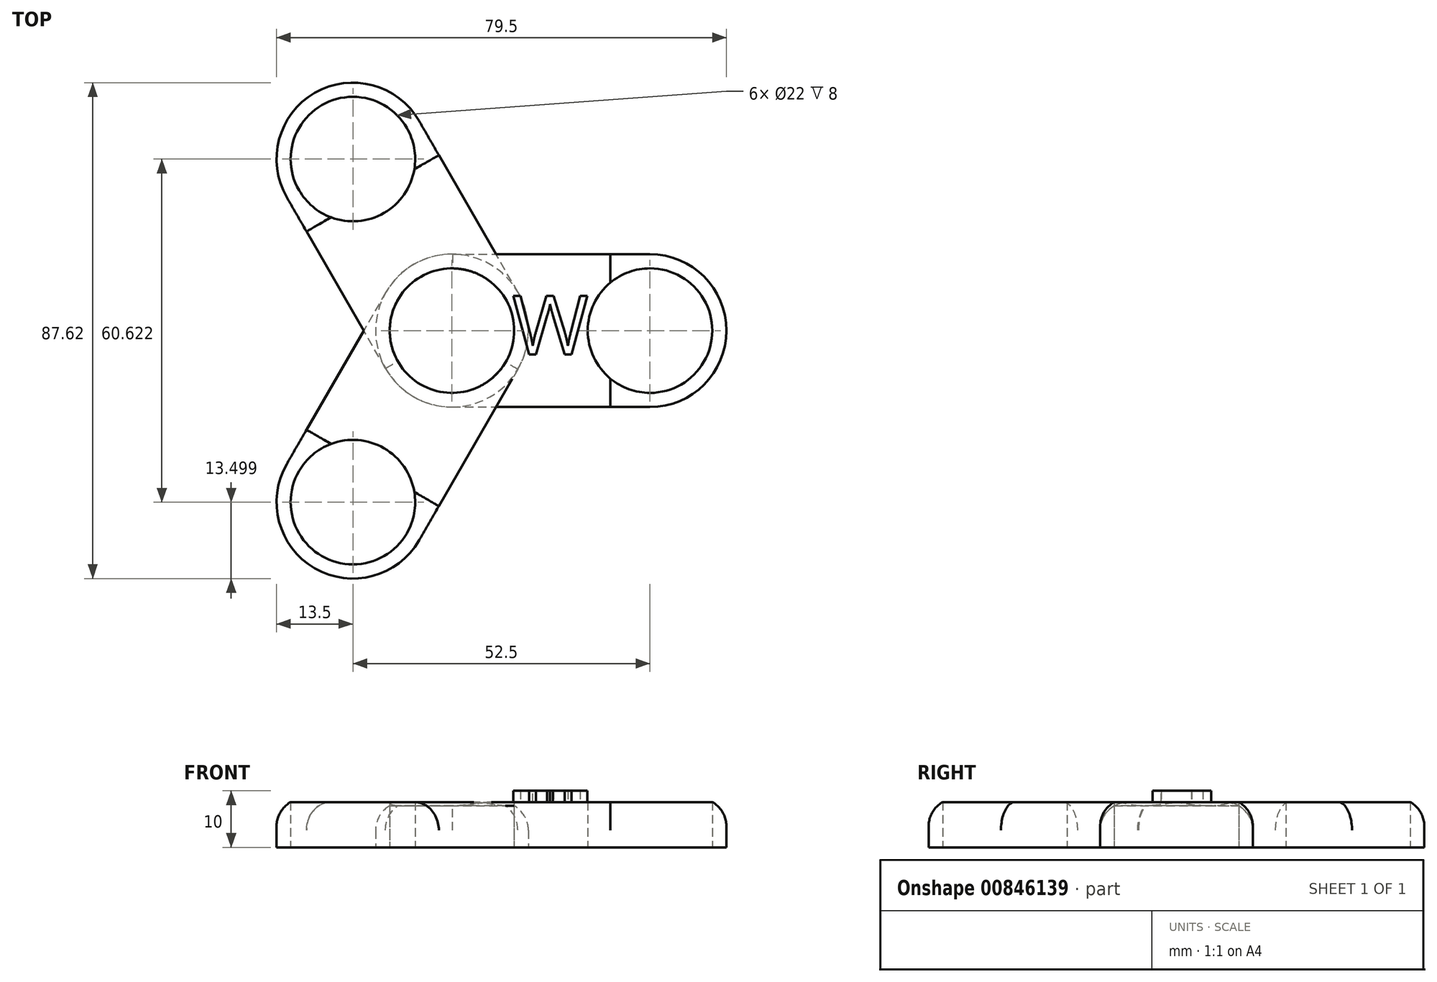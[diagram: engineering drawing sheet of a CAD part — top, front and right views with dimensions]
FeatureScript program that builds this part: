
annotation { "Feature Type Name" : "Feature", "Feature Type Description" : "" }
export const myFeature = defineFeature(function(context is Context, id is Id, definition is map)
    precondition{}
    {
        {
            var Q0;
            Q0=qCreatedBy(makeId("Top.planeOp"),FACE);
            var sketch = newSketch(context, id + "F0", { "sketchPlane" : qUnion([Q0])});
            skCircle(sketch, "E0", {"center": v(0, 0) * mm, "radius": 11 * mm});
            skCircle(sketch, "E1", {"center": v(0, 0) * mm, "radius": 13.5 * mm});
            skLineSegment(sketch, "E2", {"start": v(0, 0) * mm, "end": v(35, 0) * mm, "construction": true});
            skCircle(sketch, "E3", {"center": v(35, 0) * mm, "radius": 11 * mm});
            skCircle(sketch, "E4", {"center": v(35, 0) * mm, "radius": 13.5 * mm});
            skLineSegment(sketch, "E5", {"start": v(0.1, 13.5) * mm, "end": v(35, 13.5) * mm});
            skLineSegment(sketch, "E6", {"start": v(0, -13.5) * mm, "end": v(35, -13.5) * mm});
            skSolve(sketch);
        }
        {
            var Q0;
            Q0=makeQuery(id+"F0.imprint","IMPRINT",FACE,{"disambiguationData":[TD([[makeQuery(id+"F0.imprint","IMPRINT",EDGE,{"derivedFrom":sQuery(id+"F0.wireOp",EDGE,"E0")}),-1.0]])]});
            var Q1;
            {var subQ0=sQuery(id+"F0.wireOp",EDGE,"E5");Q1=makeQuery(id+"F0.imprint","IMPRINT",FACE,{"disambiguationData":[TD([[makeQuery(id+"F0.imprint","IMPRINT",EDGE,{"derivedFrom":subQ0}),-1.0]])]});}
            var Q2;
            Q2=makeQuery(id+"F0.imprint","IMPRINT",FACE,{"disambiguationData":[TD([[makeQuery(id+"F0.imprint","IMPRINT",EDGE,{"derivedFrom":sQuery(id+"F0.wireOp",EDGE,"E3")}),-1.0]])]});
            extrude(context, id + "F1", {"entities" : qUnion([Q0, Q1, Q2]), "depth" : 8 * mm, "offsetDistance" : 25 * mm});
        }
        {
            var Q0;
            Q0=qCreatedBy(makeId("Front.planeOp"),FACE);
            var sketch = newSketch(context, id + "F2", { "sketchPlane" : qUnion([Q0])});
            skLineSegment(sketch, "E7", {"start": v(0, 0) * mm, "end": v(0, 51.67) * mm, "construction": true});
            skSolve(sketch);
        }
        {
            var Q0;
            Q0=makeQuery(id+"F1.opExtrude","SWEPT_BODY",BODY,{"disambiguationData":[OSD([sQuery(id+"F0.wireOp",EDGE,"E0"),sQuery(id+"F0.wireOp",EDGE,"E1"),sQuery(id+"F0.wireOp",EDGE,"E3"),sQuery(id+"F0.wireOp",EDGE,"E4"),sQuery(id+"F0.wireOp",EDGE,"E5"),sQuery(id+"F0.wireOp",EDGE,"E6")])]});
            var Q1;
            Q1=sQuery(id+"F2.wireOp",EDGE,"E7");
            circularPattern(context, id + "F3", {"entities" : qUnion([Q0]), "axis" : qUnion([Q1]), "angle" : 360 * degree, "instanceCount" : 3, "equalSpace" : true});
        }
        {
            var Q0;
            Q0=makeQuery(id+"F3.opPattern","COPY",EDGE,{"derivedFrom":makeQuery(id+"F1.opExtrude","CAP_EDGE",EDGE,{"disambiguationData":[OSD([sQuery(id+"F0.wireOp",EDGE,"E5")])],"isStart":false}),"instanceName":"1"});
            var Q1;
            Q1=makeQuery(id+"F3.opPattern","COPY",EDGE,{"derivedFrom":makeQuery(id+"F1.opExtrude","CAP_EDGE",EDGE,{"disambiguationData":[OSD([sQuery(id+"F0.wireOp",EDGE,"E6")])],"isStart":false}),"instanceName":"2"});
            var Q2;
            Q2=makeQuery(id+"F1.opExtrude","CAP_EDGE",EDGE,{"disambiguationData":[OSD([sQuery(id+"F0.wireOp",EDGE,"E6")])],"isStart":false});
            fillet(context, id + "F4", {"entities" : qUnion([Q0, Q1, Q2]), "radius" : 5 * mm, "tangentPropagation" : true, "allowEdgeOverflow" : false});
        }
        {
            var Q0;
            Q0=makeQuery(id+"F1.opExtrude","CAP_FACE",FACE,{"disambiguationData":[OSD([sQuery(id+"F0.wireOp",EDGE,"E0"),sQuery(id+"F0.wireOp",EDGE,"E1"),sQuery(id+"F0.wireOp",EDGE,"E3"),sQuery(id+"F0.wireOp",EDGE,"E4"),sQuery(id+"F0.wireOp",EDGE,"E5"),sQuery(id+"F0.wireOp",EDGE,"E6")])],"isStart":false});
            var sketch = newSketch(context, id + "F5", { "sketchPlane" : qUnion([Q0])});
            skText(sketch, "E8", { "text": "W", "fontName": "OpenSans-Regular.ttf"});
            const initialGuessF5  = {"E8": [0.01068, -0.00424, 1, 0, 0.01044]};
            skSetInitialGuess(sketch, initialGuessF5);
            skSolve(sketch);
        }
        {
            var Q0;
            Q0 = qSketchRegion(id + "F5", true);
            extrude(context, id + "F6", {"entities" : qUnion([Q0]), "operationType" : NewBodyOperationType.ADD, "depth" : 2 * mm, "offsetDistance" : 25 * mm});
        }
    });
